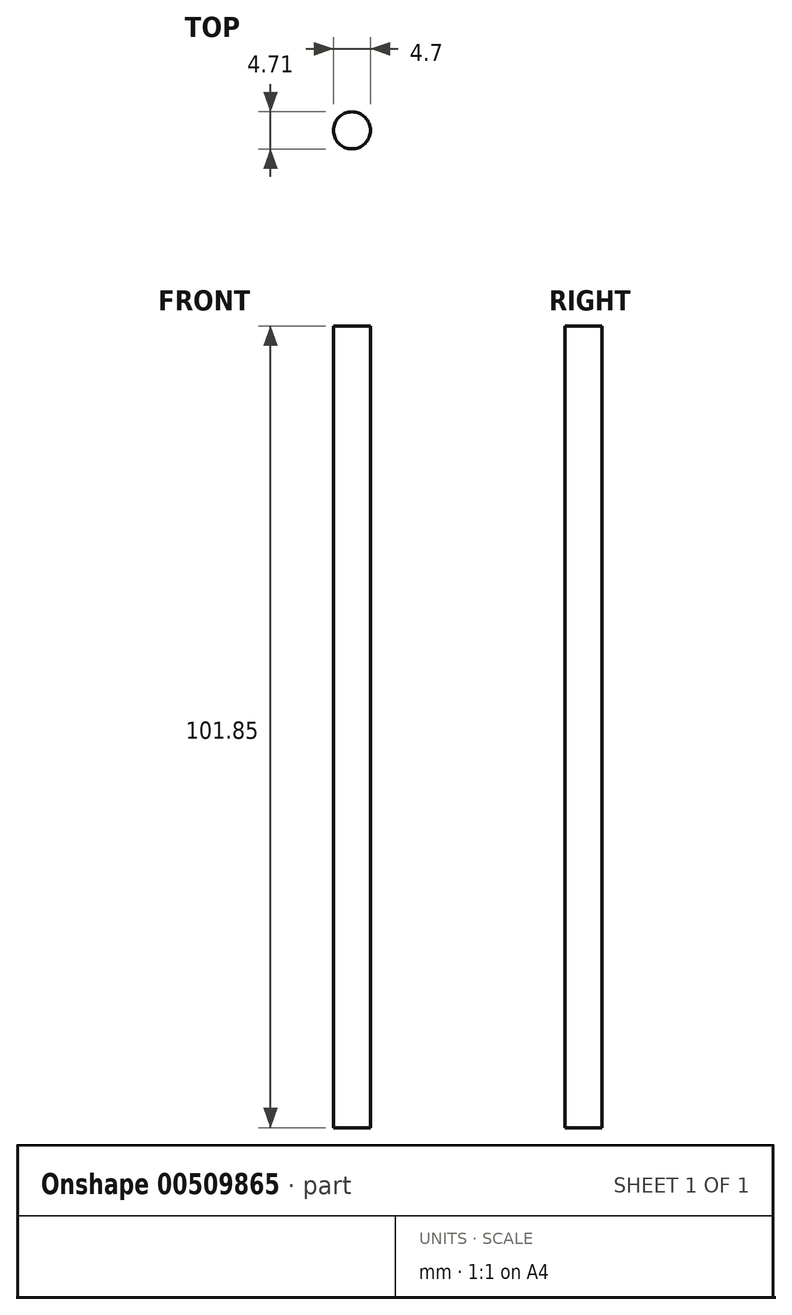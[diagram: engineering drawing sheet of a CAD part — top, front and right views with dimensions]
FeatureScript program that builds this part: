
annotation { "Feature Type Name" : "Feature", "Feature Type Description" : "" }
export const myFeature = defineFeature(function(context is Context, id is Id, definition is map)
    precondition{}
    {
        {
            var Q0;
            Q0=qCreatedBy(makeId("Top.planeOp"),FACE);
            var sketch = newSketch(context, id + "F0", { "sketchPlane" : qUnion([Q0])});
            skCircle(sketch, "E0", {"center": v(0, 40.69) * mm, "radius": 2.35 * mm});
            skSolve(sketch);
        }
        {
            var Q0;
            Q0 = qSketchRegion(id + "F0", true);
            extrude(context, id + "F1", {"entities" : qUnion([Q0]), "depth" : 101.85 * mm});
        }
        {
            var Q0;
            Q0=qCreatedBy(makeId("Right.planeOp"),FACE);
            var sketch = newSketch(context, id + "F2", { "sketchPlane" : qUnion([Q0])});
            skLineSegment(sketch, "E1", {"start": v(40.7, 101.37) * mm, "end": v(40.7, 0) * mm});
            skLineSegment(sketch, "E2", {"start": v(40.7, 0) * mm, "end": v(16.22, 0) * mm});
            skLineSegment(sketch, "E3", {"start": v(16.22, 0) * mm, "end": v(16.22, 31.18) * mm});
            skLineSegment(sketch, "E4", {"start": v(16.22, 31.18) * mm, "end": v(-26.96, 34.23) * mm});
            skLineSegment(sketch, "E5", {"start": v(-26.96, 34.23) * mm, "end": v(-24, 76.05) * mm});
            skLineSegment(sketch, "E6", {"start": v(-24, 76.05) * mm, "end": v(18.3, 76.05) * mm});
            skLineSegment(sketch, "E7", {"start": v(18.3, 76.05) * mm, "end": v(18.3, 100.25) * mm});
            skLineSegment(sketch, "E8", {"start": v(18.3, 100.25) * mm, "end": v(40.7, 101.37) * mm});
            skSolve(sketch);
        }
    });
